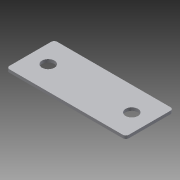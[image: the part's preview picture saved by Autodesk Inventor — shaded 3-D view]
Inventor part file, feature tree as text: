
AUTODESK INVENTOR PART (.ipt)
format: ipt  version: 2013 (Build 170138000, 138)  size: 85,504 bytes
history: native  units: in
note: dims shown in document units (in); Inventor stores cm internally (conversion verified against a paired STEP export)
features: extrude x1, fillet x1, sketch x1
ambient origin geometry x8: Origin, YZ Plane, XZ Plane, XY Plane, X Axis, Y Axis, Z Axis, Center Point
bodies: Solid1 (feature_tree)
feature tree (3):
  extrude  "Extrusion1"  Depth=1.0in
  fillet  "Fillet1"  Radius=1.75in
  sketch  "Sketch1"  dims[d0=2.5in d2=1.0in d3=1.75in d4=0.26in d5=0.0625in d6=0.0in d7=0.0625in]
